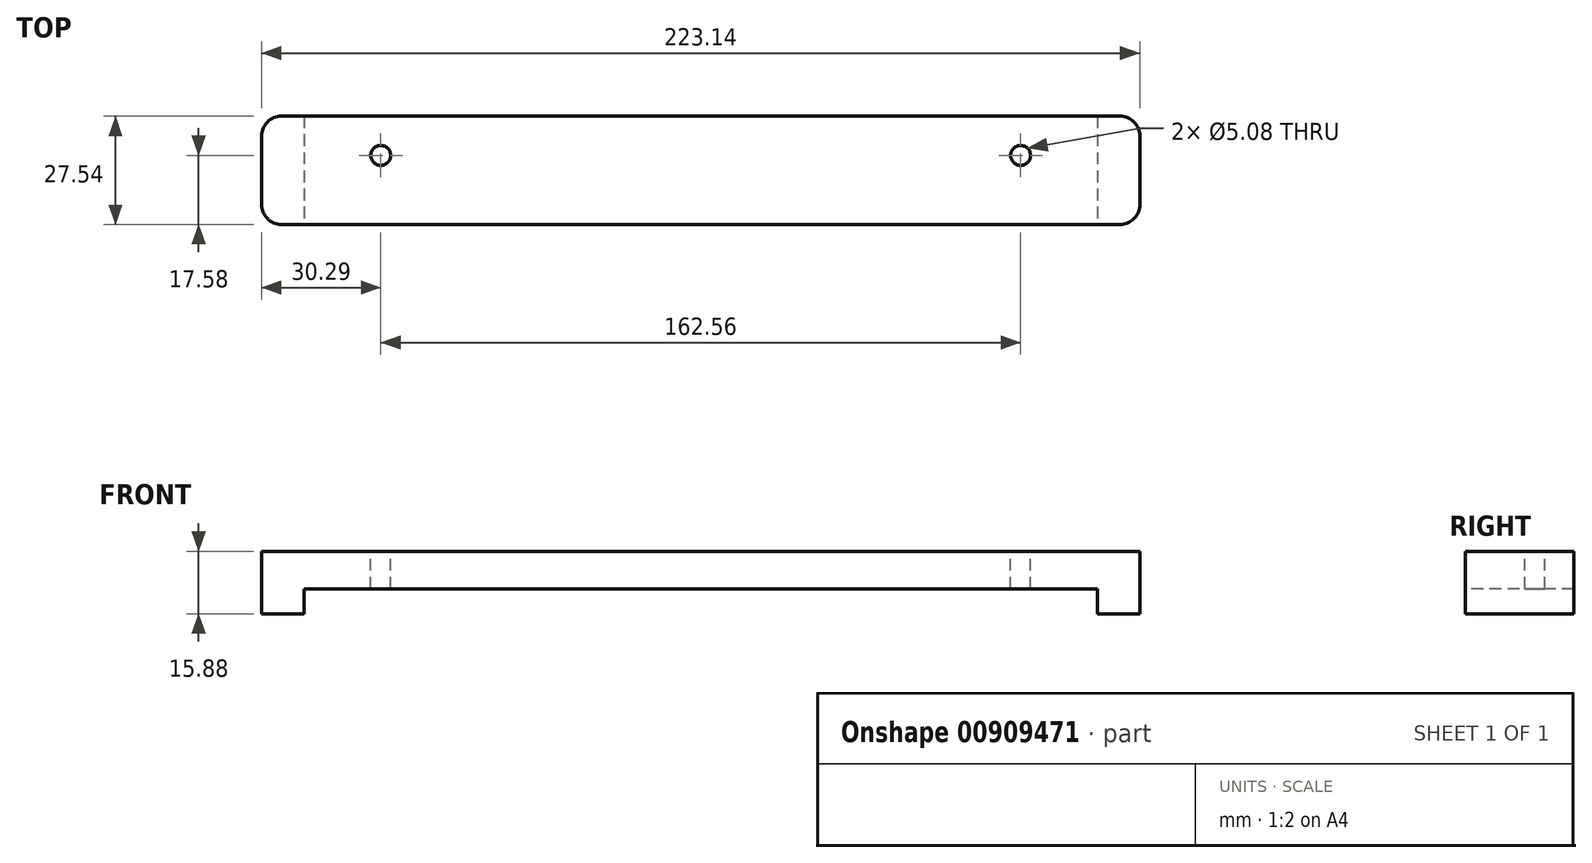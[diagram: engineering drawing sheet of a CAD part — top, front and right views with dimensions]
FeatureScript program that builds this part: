
annotation { "Feature Type Name" : "Feature", "Feature Type Description" : "" }
export const myFeature = defineFeature(function(context is Context, id is Id, definition is map)
    precondition{}
    {
        {
            var Q0;
            Q0=qCreatedBy(makeId("Top.planeOp"),FACE);
            var sketch = newSketch(context, id + "F0", { "sketchPlane" : qUnion([Q0])});
            skLineSegment(sketch, "E0", {"start": v(-111.77, 15.24) * mm, "end": v(-111.77, 0) * mm, "construction": true});
            skLineSegment(sketch, "E1", {"start": v(111.77, 15.24) * mm, "end": v(111.77, 0) * mm, "construction": true});
            skLineSegment(sketch, "E2", {"start": v(111.77, 0) * mm, "end": v(-111.77, 0) * mm, "construction": true});
            skLineSegment(sketch, "E3", {"start": v(-111.77, 15.24) * mm, "end": v(111.77, 15.24) * mm, "construction": true});
            skLineSegment(sketch, "E4.0", {"start": v(-111.57, 15.04) * mm, "end": v(-111.57, 0.2) * mm});
            skLineSegment(sketch, "E4.1", {"start": v(111.57, 15.04) * mm, "end": v(111.57, 0.2) * mm});
            skLineSegment(sketch, "E4.3", {"start": v(-111.57, 15.04) * mm, "end": v(111.57, 15.04) * mm});
            skLineSegment(sketch, "E4.4", {"start": v(111.57, 0.2) * mm, "end": v(-111.57, 0.2) * mm});
            skSolve(sketch);
        }
        {
            var Q0;
            Q0=qSketchRegion(id+"F0",true);
            extrude(context, id + "F1", {"entities" : qUnion([Q0]), "depth" : 9.52 * mm, "offsetDistance" : 25.4 * mm});
        }
        {
            var Q0;
            Q0=makeQuery(id+"F1.opExtrude","CAP_FACE",FACE,{"disambiguationData":[OSD([sQuery(id+"F0.wireOp",EDGE,"E4.0"),sQuery(id+"F0.wireOp",EDGE,"E4.1"),sQuery(id+"F0.wireOp",EDGE,"E4.2"),sQuery(id+"F0.wireOp",EDGE,"E4.3"),sQuery(id+"F0.wireOp",EDGE,"E4.4"),sQuery(id+"F0.wireOp",EDGE,"E4.5")])],"isStart":false});
            var sketch = newSketch(context, id + "F2", { "sketchPlane" : qUnion([Q0])});
            skCircle(sketch, "E5", {"center": v(-81.28, 5.08) * mm, "radius": 2.54 * mm});
            skCircle(sketch, "E6", {"center": v(81.28, 5.08) * mm, "radius": 2.54 * mm});
            skLineSegment(sketch, "E7", {"start": v(-81.28, 5.08) * mm, "end": v(81.28, 5.08) * mm, "construction": true});
            skLineSegment(sketch, "E8", {"start": v(0, 0.82) * mm, "end": v(0, 5.08) * mm, "construction": true});
            skSolve(sketch);
        }
        {
            var Q0;
            Q0=qSketchRegion(id+"F2",true);
            extrude(context, id + "F3", {"entities" : qUnion([Q0]), "operationType" : NewBodyOperationType.REMOVE, "endBound" : BoundingType.THROUGH_ALL, "oppositeDirection" : true, "depth" : 25.4 * mm, "offsetDistance" : 25.4 * mm});
        }
        {
            var Q0;
            Q0=makeQuery(id+"F1.opExtrude","CAP_FACE",FACE,{"disambiguationData":[OSD([sQuery(id+"F0.wireOp",EDGE,"E4.0"),sQuery(id+"F0.wireOp",EDGE,"E4.1"),sQuery(id+"F0.wireOp",EDGE,"E4.3"),sQuery(id+"F0.wireOp",EDGE,"E4.4")])],"isStart":true});
            var sketch = newSketch(context, id + "F4", { "sketchPlane" : qUnion([Q0])});
            skLineSegment(sketch, "E9.bottom", {"start": v(-111.57, -15.04) * mm, "end": v(-100.77, -15.04) * mm});
            skLineSegment(sketch, "E9.top", {"start": v(-111.57, -0.2) * mm, "end": v(-100.77, -0.2) * mm});
            skLineSegment(sketch, "E9.left", {"start": v(-111.57, -15.04) * mm, "end": v(-111.57, -0.2) * mm});
            skLineSegment(sketch, "E9.right", {"start": v(-100.77, -15.04) * mm, "end": v(-100.77, -0.2) * mm});
            skLineSegment(sketch, "E10.bottom", {"start": v(111.57, -15.04) * mm, "end": v(100.77, -15.04) * mm});
            skLineSegment(sketch, "E10.top", {"start": v(111.57, -0.2) * mm, "end": v(100.77, -0.2) * mm});
            skLineSegment(sketch, "E10.left", {"start": v(111.57, -15.04) * mm, "end": v(111.57, -0.2) * mm});
            skLineSegment(sketch, "E10.right", {"start": v(100.77, -15.04) * mm, "end": v(100.77, -0.2) * mm});
            skSolve(sketch);
        }
        {
            var Q0;
            Q0 = qSketchRegion(id + "F4", true);
            extrude(context, id + "F5", {"entities" : qUnion([Q0]), "operationType" : NewBodyOperationType.ADD, "depth" : 6.35 * mm, "offsetDistance" : 25.4 * mm});
        }
        {
            var Q0;
            Q0=makeQuery(id+"F5.boolean.opBoolean","MERGE",FACE,{"derivedFrom":[makeQuery(id+"F1.opExtrude","SWEPT_FACE",FACE,{"disambiguationData":[OSD([sQuery(id+"F0.wireOp",EDGE,"E4.4")])]}),makeQuery(id+"F5.opExtrude","SWEPT_FACE",FACE,{"disambiguationData":[OSD([sQuery(id+"F4.wireOp",EDGE,"E9.top")])]}),makeQuery(id+"F5.opExtrude","SWEPT_FACE",FACE,{"disambiguationData":[OSD([sQuery(id+"F4.wireOp",EDGE,"E10.top")])]})]});
            var sketch = newSketch(context, id + "F6", { "sketchPlane" : qUnion([Q0])});
            skLineSegment(sketch, "E11", {"start": v(111.57, -6.35) * mm, "end": v(111.57, 9.53) * mm});
            skLineSegment(sketch, "E12", {"start": v(111.57, 9.53) * mm, "end": v(-111.57, 9.53) * mm});
            skLineSegment(sketch, "E13", {"start": v(-111.57, 9.53) * mm, "end": v(-111.57, -6.35) * mm});
            skLineSegment(sketch, "E14", {"start": v(-111.57, -6.35) * mm, "end": v(-100.77, -6.35) * mm});
            skLineSegment(sketch, "E15", {"start": v(-100.77, -6.35) * mm, "end": v(-100.77, 0) * mm});
            skLineSegment(sketch, "E16", {"start": v(-100.77, 0) * mm, "end": v(100.77, 0) * mm});
            skLineSegment(sketch, "E17", {"start": v(100.77, 0) * mm, "end": v(100.77, -6.35) * mm});
            skLineSegment(sketch, "E18", {"start": v(100.77, -6.35) * mm, "end": v(111.57, -6.35) * mm});
            skSolve(sketch);
        }
        {
            var Q0;
            Q0 = qSketchRegion(id + "F6", true);
            extrude(context, id + "F7", {"entities" : qUnion([Q0]), "operationType" : NewBodyOperationType.ADD, "depth" : 12.7 * mm, "offsetDistance" : 25.4 * mm});
        }
        {
            var Q0;
            Q0=makeQuery(id+"F7.opExtrude","CAP_EDGE",EDGE,{"disambiguationData":[OSD([sQuery(id+"F6.wireOp",EDGE,"E11")])],"isStart":false});
            var Q1;
            Q1=makeQuery(id+"F5.boolean.opBoolean","MERGE",EDGE,{"derivedFrom":[makeQuery(id+"F1.opExtrude","SWEPT_EDGE",EDGE,{"disambiguationData":[OSD([sQuery(id+"F0.wireOp",EDGE,"E4.1"),sQuery(id+"F0.wireOp",EDGE,"E4.3")])]}),makeQuery(id+"F5.opExtrude","SWEPT_EDGE",EDGE,{"disambiguationData":[OSD([sQuery(id+"F4.wireOp",EDGE,"E10.bottom"),sQuery(id+"F4.wireOp",EDGE,"E10.left")])]})]});
            var Q2;
            Q2=makeQuery(id+"F7.opExtrude","CAP_EDGE",EDGE,{"disambiguationData":[OSD([sQuery(id+"F6.wireOp",EDGE,"E13")])],"isStart":false});
            var Q3;
            Q3=makeQuery(id+"F5.boolean.opBoolean","MERGE",EDGE,{"derivedFrom":[makeQuery(id+"F1.opExtrude","SWEPT_EDGE",EDGE,{"disambiguationData":[OSD([sQuery(id+"F0.wireOp",EDGE,"E4.0"),sQuery(id+"F0.wireOp",EDGE,"E4.3")])]}),makeQuery(id+"F5.opExtrude","SWEPT_EDGE",EDGE,{"disambiguationData":[OSD([sQuery(id+"F4.wireOp",EDGE,"E9.bottom"),sQuery(id+"F4.wireOp",EDGE,"E9.left")])]})]});
            fillet(context, id + "F8", {"entities" : qUnion([Q0, Q1, Q2, Q3]), "radius" : 5.08 * mm, "tangentPropagation" : true, "allowEdgeOverflow" : false});
        }
    });
